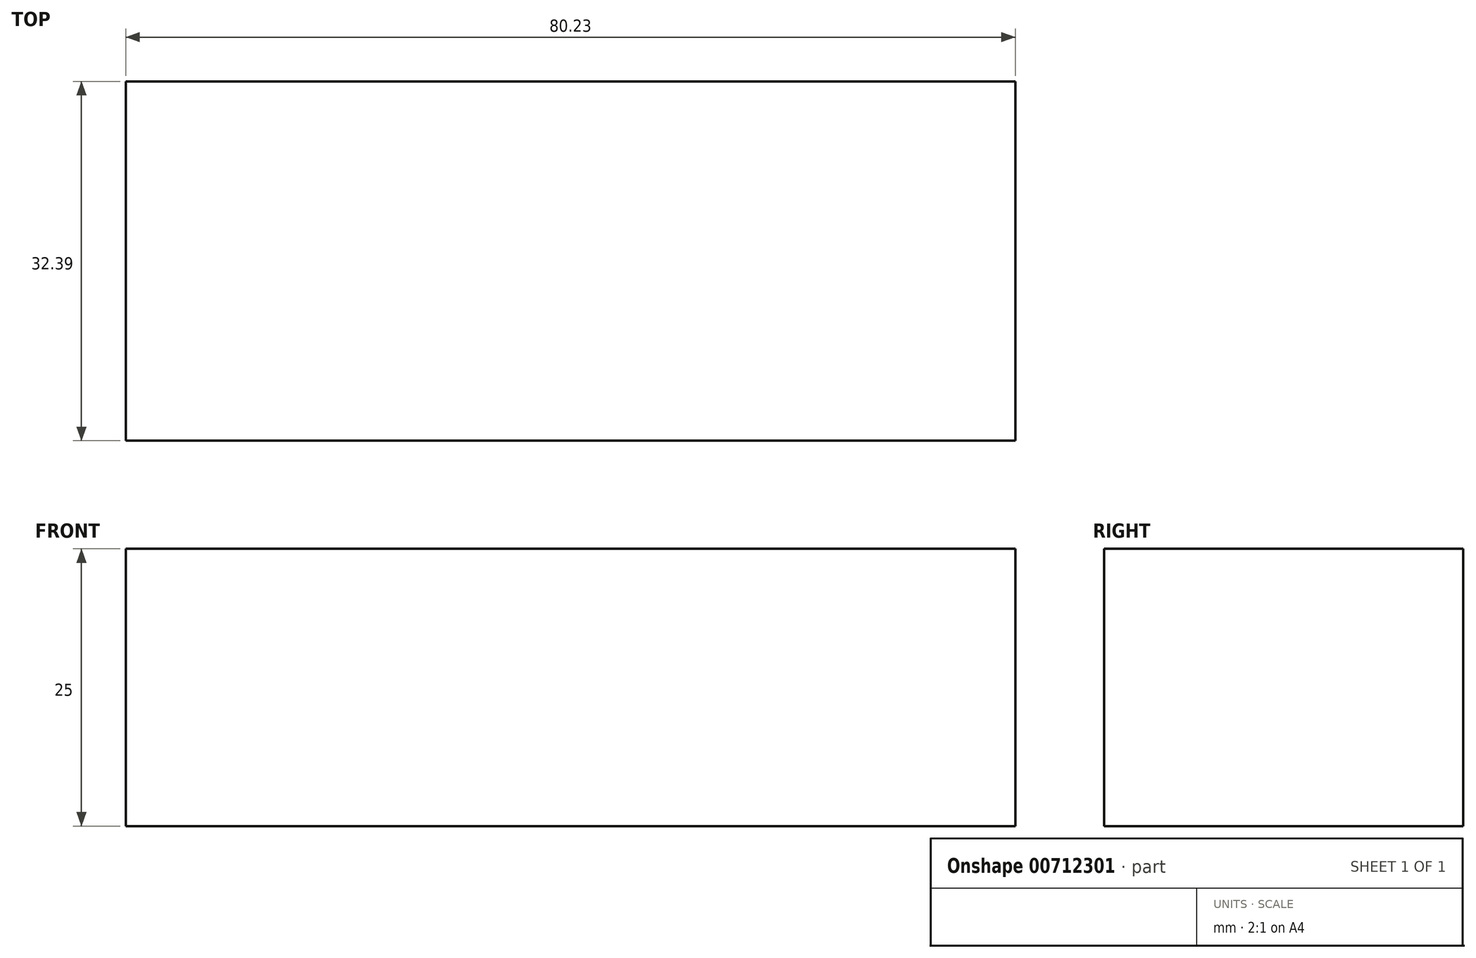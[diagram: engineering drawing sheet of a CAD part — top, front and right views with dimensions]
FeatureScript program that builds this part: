
annotation { "Feature Type Name" : "Feature", "Feature Type Description" : "" }
export const myFeature = defineFeature(function(context is Context, id is Id, definition is map)
    precondition{}
    {
        {
            var Q0;
            Q0=qCreatedBy(makeId("Top.planeOp"),FACE);
            var sketch = newSketch(context, id + "F0", { "sketchPlane" : qUnion([Q0])});
            skLineSegment(sketch, "E0.bottom", {"start": v(-57.43, 29.18) * mm, "end": v(22.8, 29.18) * mm});
            skLineSegment(sketch, "E0.top", {"start": v(-57.43, -3.21) * mm, "end": v(22.8, -3.21) * mm});
            skLineSegment(sketch, "E0.left", {"start": v(-57.43, 29.18) * mm, "end": v(-57.43, -3.21) * mm});
            skLineSegment(sketch, "E0.right", {"start": v(22.8, 29.18) * mm, "end": v(22.8, -3.21) * mm});
            skLineSegment(sketch, "E1.left", {"start": v(-57.43, 29.18) * mm, "end": v(-57.43, 29.18) * mm});
            skLineSegment(sketch, "E1.right", {"start": v(22.8, 29.18) * mm, "end": v(22.8, 29.18) * mm});
            skSolve(sketch);
        }
        {
            var Q0;
            Q0 = qSketchRegion(id + "F0", true);
            extrude(context, id + "F1", {"entities" : qUnion([Q0]), "depth" : 25 * mm, "offsetDistance" : 25 * mm});
        }
    });
